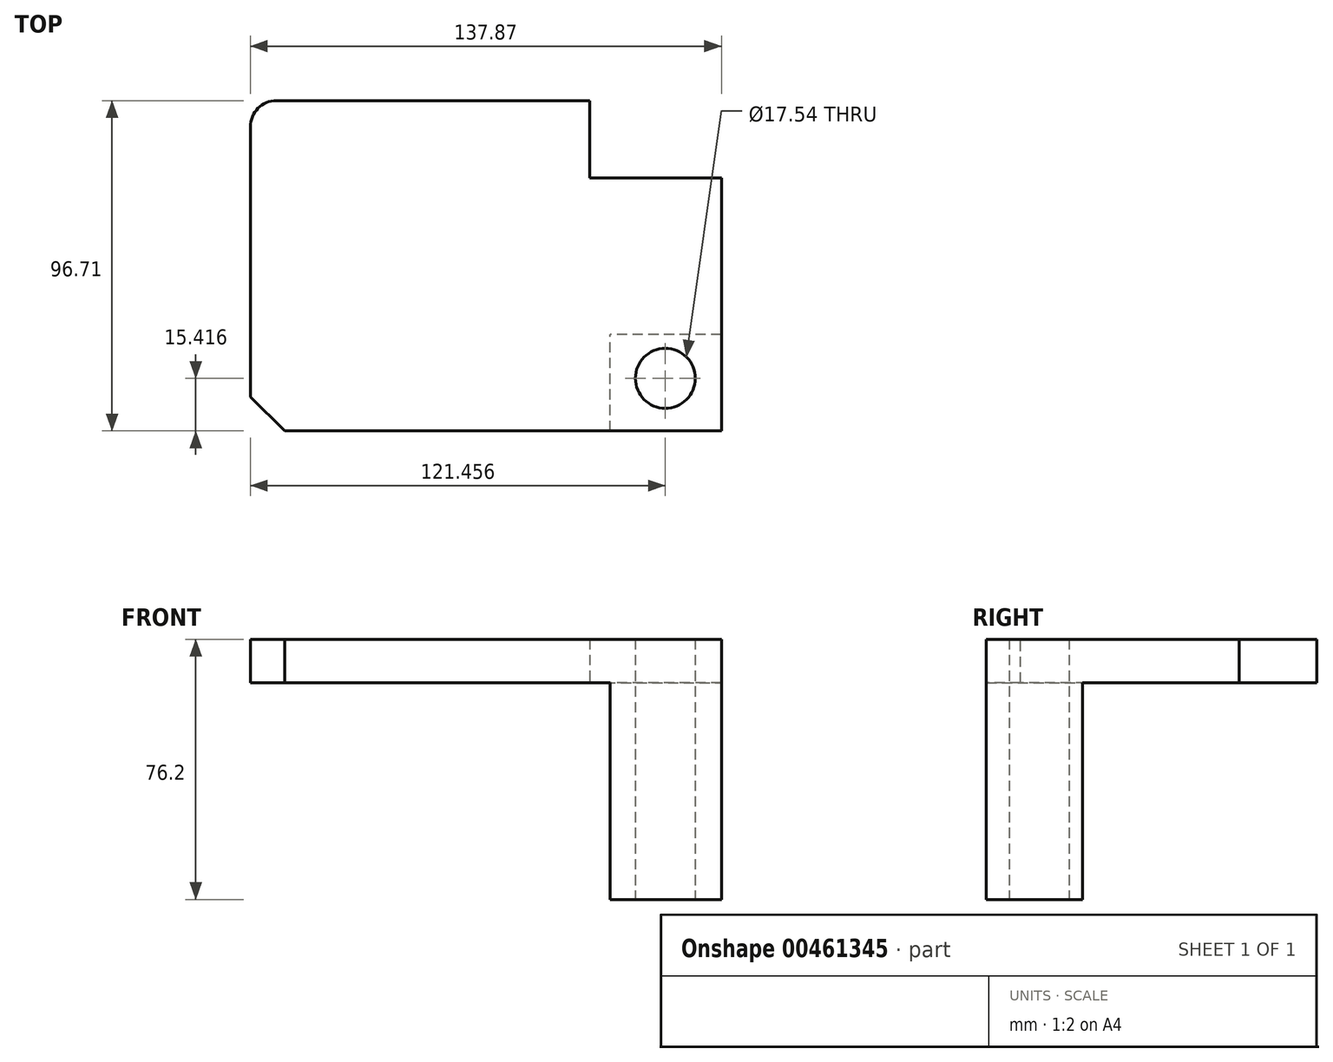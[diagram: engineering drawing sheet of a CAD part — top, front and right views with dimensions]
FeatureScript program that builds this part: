
annotation { "Feature Type Name" : "Feature", "Feature Type Description" : "" }
export const myFeature = defineFeature(function(context is Context, id is Id, definition is map)
    precondition{}
    {
        {
            var Q0;
            Q0=qCreatedBy(makeId("Top.planeOp"),FACE);
            var sketch = newSketch(context, id + "F0", { "sketchPlane" : qUnion([Q0])});
            skLineSegment(sketch, "E0.bottom", {"start": v(-43.27, 37) * mm, "end": v(94.6, 37) * mm});
            skLineSegment(sketch, "E0.top", {"start": v(-43.27, -59.72) * mm, "end": v(94.6, -59.72) * mm});
            skLineSegment(sketch, "E0.left", {"start": v(-43.27, 37) * mm, "end": v(-43.27, -59.72) * mm});
            skLineSegment(sketch, "E0.right", {"start": v(94.6, 37) * mm, "end": v(94.6, -59.72) * mm});
            skLineSegment(sketch, "E1.bottom", {"start": v(94.6, -59.72) * mm, "end": v(69.86, -59.72) * mm});
            skLineSegment(sketch, "E1.left", {"start": v(94.6, -59.72) * mm, "end": v(94.6, -27.48) * mm});
            skLineSegment(sketch, "E2.bottom", {"start": v(94.6, -59.72) * mm, "end": v(58.5, -59.72) * mm});
            skLineSegment(sketch, "E2.left", {"start": v(94.6, -59.72) * mm, "end": v(94.6, -27.07) * mm});
            skSolve(sketch);
        }
        {
            var Q0;
            Q0 = qSketchRegion(id + "F0", true);
            extrude(context, id + "F1", {"entities" : qUnion([Q0]), "depth" : 12.7 * mm});
        }
        {
            var Q0;
            Q0=makeQuery(id+"F1.opExtrude","CAP_FACE",FACE,{"disambiguationData":[OSD([sQuery(id+"F0.wireOp",EDGE,"E0.bottom"),sQuery(id+"F0.wireOp",EDGE,"E0.top"),sQuery(id+"F0.wireOp",EDGE,"E0.left"),sQuery(id+"F0.wireOp",EDGE,"E0.right"),sQuery(id+"F0.wireOp",EDGE,"E2.bottom"),sQuery(id+"F0.wireOp",EDGE,"E2.left")])],"isStart":false});
            var sketch = newSketch(context, id + "F2", { "sketchPlane" : qUnion([Q0])});
            skLineSegment(sketch, "E3.bottom", {"start": v(94.6, -59.72) * mm, "end": v(61.96, -59.72) * mm});
            skLineSegment(sketch, "E3.top", {"start": v(94.6, -31.52) * mm, "end": v(61.96, -31.52) * mm});
            skLineSegment(sketch, "E3.left", {"start": v(94.6, -59.72) * mm, "end": v(94.6, -31.52) * mm});
            skLineSegment(sketch, "E3.right", {"start": v(61.96, -59.72) * mm, "end": v(61.96, -31.52) * mm});
            skSolve(sketch);
        }
        {
            var Q0;
            Q0 = qSketchRegion(id + "F2", true);
            extrude(context, id + "F3", {"entities" : qUnion([Q0]), "operationType" : NewBodyOperationType.ADD, "oppositeDirection" : true, "depth" : 76.2 * mm});
        }
        {
            var Q0;
            Q0=makeQuery(id+"F3.boolean.opBoolean","MERGE",FACE,{"derivedFrom":[makeQuery(id+"F1.opExtrude","SWEPT_FACE",FACE,{"disambiguationData":[OSD([sQuery(id+"F0.wireOp",EDGE,"E0.right"),sQuery(id+"F0.wireOp",EDGE,"E2.left")])]}),makeQuery(id+"F3.opExtrude","SWEPT_FACE",FACE,{"disambiguationData":[OSD([sQuery(id+"F2.wireOp",EDGE,"E3.left")])]})]});
            var sketch = newSketch(context, id + "F4", { "sketchPlane" : qUnion([Q0])});
            skLineSegment(sketch, "E4", {"start": v(14.33, 12.7) * mm, "end": v(14.33, 0) * mm});
            skSolve(sketch);
        }
        {
            var Q0;
            {var subQ0=sQuery(id+"F4.wireOp",EDGE,"E4");Q0=makeQuery(id+"F4.imprint","IMPRINT",FACE,{"disambiguationData":[TD([[makeQuery(id+"F4.imprint","IMPRINT",EDGE,{"derivedFrom":subQ0}),1.0]])]});}
            extrude(context, id + "F5", {"entities" : qUnion([Q0]), "operationType" : NewBodyOperationType.REMOVE, "oppositeDirection" : true, "depth" : 38.6 * mm});
        }
        {
            var Q0;
            Q0=makeQuery(id+"F3.opExtrude","CAP_FACE",FACE,{"disambiguationData":[OSD([sQuery(id+"F2.wireOp",EDGE,"E3.bottom"),sQuery(id+"F2.wireOp",EDGE,"E3.top"),sQuery(id+"F2.wireOp",EDGE,"E3.left"),sQuery(id+"F2.wireOp",EDGE,"E3.right")])],"isStart":false});
            var sketch = newSketch(context, id + "F6", { "sketchPlane" : qUnion([Q0])});
            skCircle(sketch, "E5", {"center": v(78.19, 44.3) * mm, "radius": 8.77 * mm});
            skSolve(sketch);
        }
        {
            var Q0;
            Q0 = qSketchRegion(id + "F6", true);
            extrude(context, id + "F7", {"entities" : qUnion([Q0]), "operationType" : NewBodyOperationType.REMOVE, "oppositeDirection" : true, "depth" : 76.2 * mm});
        }
        {
            var Q0;
            Q0=makeQuery(id+"F1.opExtrude","SWEPT_EDGE",EDGE,{"disambiguationData":[OSD([sQuery(id+"F0.wireOp",EDGE,"E0.bottom"),sQuery(id+"F0.wireOp",EDGE,"E0.left")])]});
            fillet(context, id + "F8", {"entities" : qUnion([Q0]), "radius" : 7.62 * mm, "tangentPropagation" : true, "allowEdgeOverflow" : false});
        }
        {
            var Q0;
            Q0=makeQuery(id+"F1.opExtrude","SWEPT_EDGE",EDGE,{"disambiguationData":[OSD([sQuery(id+"F0.wireOp",EDGE,"E0.top"),sQuery(id+"F0.wireOp",EDGE,"E0.left")])]});
            chamfer(context, id + "F9", {"entities" : qUnion([Q0]), "width" : 10 * mm, "tangentPropagation" : true});
        }
    });
